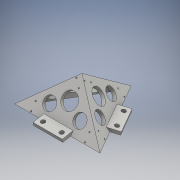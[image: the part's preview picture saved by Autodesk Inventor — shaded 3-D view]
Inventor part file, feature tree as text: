
AUTODESK INVENTOR PART (.ipt)
format: ipt  version: 2016 (Build 200138000, 138)  size: 271,872 bytes
history: native  units: mm
features: sketch x7, plane x4, extrude x4, pattern_circular x4, hole x2, other x1, projected_geometry x1
ambient origin geometry x8: Origin, YZ Plane, XZ Plane, XY Plane, X Axis, Y Axis, Z Axis, Center Point
bodies: Solid1 (feature_tree)
feature tree (23):
  sketch  "Sketch1"  dims[d0=82.0mm d1=82.0mm]
  other  "Work Axis1"
  sketch  "Sketch2"  dims[d2=82.0mm]
  plane  "Work Plane2"
  extrude  "Extrusion1"  Depth=82.0mm
  pattern_circular  "Circular Pattern1"  Count=3 Angle=360.0deg
  sketch  "Sketch4"  dims[d4=3.0mm d5=-7.853982mm d6=30.0mm d7=360.0deg]
  hole  "Hole2"  [1 undecoded]
  pattern_circular  "Circular Pattern2"  Count=3 Angle=360.0deg
  extrude  "Extrusion3"  Depth=10.0mm
  extrude  "Extrusion2"  Depth=10.0mm
  pattern_circular  "Circular Pattern4"  [2 undecoded]
  plane  "Work Plane4"
  extrude  "Extrusion4"  Depth=5.0mm TaperAngle=0.0deg
  hole  "Hole3"  [1 undecoded]
  pattern_circular  "Circular Pattern5"  [2 undecoded]
  plane  "Work Plane1"
  sketch  "Sketch3"  dims[d3=34.0mm]
  projected_geometry  "Projected Loop1"
  sketch  "Sketch5"  dims[d10=7.62mm d11=1.27mm]
  sketch  "Sketch7"  dims[d19=1.181mm d20=3.048mm d21=4.0mm d22=2.0mm d23=90.0deg d24=4.636mm d25=20.594885mm d26=30.0mm d27=360.0deg]
  plane  "Work Plane3"
  sketch  "Sketch9"  dims[d29=7.62mm d30=15.0mm d31=12.0mm d32=12.0mm d33=5.0mm d34=0.0mm d42=12.0mm d43=28.0mm d44=4.0mm d45=4.0mm d46=5.0mm d47=5.0mm d48=3.0mm d49=0.0mm d50=2.5mm d51=0.0mm d52=30.0mm d53=360.0deg d55=23.0mm d56=10.0mm d57=0.0mm d58=10.16mm d59=5.08mm d60=1.27mm d61=10.16mm d62=10.16mm d63=10.16mm d64=5.08mm d65=1.27mm d66=1.181mm d67=3.048mm d68=4.0mm d69=2.0mm d70=90.0deg d71=4.636mm d72=20.594885mm d73=30.0mm d74=360.0deg]
note: 6 required parameter values undecoded (feature->parameter linkage not recoverable at this tier; creation-order binding heuristic only, values carry confidence <= 0.55)
